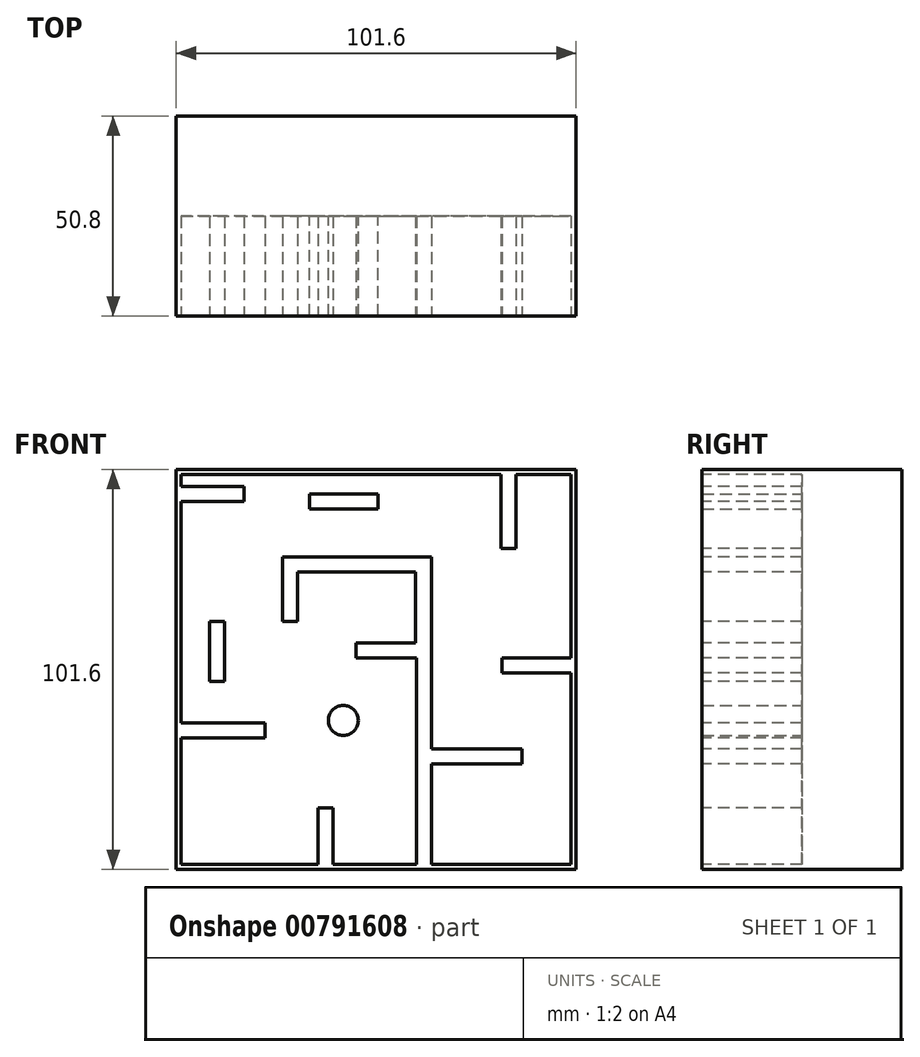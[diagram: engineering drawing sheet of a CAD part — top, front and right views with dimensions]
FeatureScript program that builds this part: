
annotation { "Feature Type Name" : "Feature", "Feature Type Description" : "" }
export const myFeature = defineFeature(function(context is Context, id is Id, definition is map)
    precondition{}
    {
        {
            var Q0;
            Q0=qCreatedBy(makeId("Front.planeOp"),FACE);
            var sketch = newSketch(context, id + "F0", { "sketchPlane" : qUnion([Q0])});
            skLineSegment(sketch, "E0.bottom", {"start": v(-45.67, 38.55) * mm, "end": v(55.93, 38.55) * mm});
            skLineSegment(sketch, "E0.top", {"start": v(-45.67, -63.05) * mm, "end": v(55.93, -63.05) * mm});
            skLineSegment(sketch, "E0.left", {"start": v(-45.67, 38.55) * mm, "end": v(-45.67, -63.05) * mm});
            skLineSegment(sketch, "E0.right", {"start": v(55.93, 38.55) * mm, "end": v(55.93, -63.05) * mm});
            skSolve(sketch);
        }
        {
            var Q0;
            Q0 = qSketchRegion(id + "F0", true);
            extrude(context, id + "F1", {"entities" : qUnion([Q0]), "depth" : 50.8 * mm, "offsetDistance" : 25.4 * mm});
        }
        {
            var Q0;
            Q0=makeQuery(id+"F1.opExtrude","CAP_FACE",FACE,{"disambiguationData":[OSD([sQuery(id+"F0.wireOp",EDGE,"E0.bottom"),sQuery(id+"F0.wireOp",EDGE,"E0.top"),sQuery(id+"F0.wireOp",EDGE,"E0.left"),sQuery(id+"F0.wireOp",EDGE,"E0.right")])],"isStart":false});
            var sketch = newSketch(context, id + "F2", { "sketchPlane" : qUnion([Q0])});
            skPoint(sketch, "E1.end.orphan", {"position": v(-45.67, -36.4) * mm});
            skLineSegment(sketch, "E2", {"start": v(-9.62, -63.05) * mm, "end": v(-9.62, -47.4) * mm});
            skPoint(sketch, "E2.startSnap0", {"position": v(-9.62, -34.5) * mm});
            skLineSegment(sketch, "E3", {"start": v(-9.62, -47.4) * mm, "end": v(-5.8, -47.4) * mm});
            skLineSegment(sketch, "E4", {"start": v(-5.8, -47.4) * mm, "end": v(-5.8, -63.05) * mm});
            skLineSegment(sketch, "E5", {"start": v(0, -9.31) * mm, "end": v(15.4, -9.31) * mm});
            skLineSegment(sketch, "E6", {"start": v(19.22, -9.31) * mm, "end": v(19.22, 16.32) * mm});
            skLineSegment(sketch, "E7", {"start": v(19.22, 16.32) * mm, "end": v(-18.6, 16.32) * mm});
            skLineSegment(sketch, "E8", {"start": v(-18.6, 16.32) * mm, "end": v(-18.6, 0) * mm});
            skLineSegment(sketch, "E9", {"start": v(0, -9.31) * mm, "end": v(0, -5.5) * mm});
            skLineSegment(sketch, "E10", {"start": v(0, -5.5) * mm, "end": v(15.1, -5.5) * mm});
            skLineSegment(sketch, "E11", {"start": v(15.1, -5.5) * mm, "end": v(15.1, 12.51) * mm});
            skLineSegment(sketch, "E12", {"start": v(15.1, 12.51) * mm, "end": v(-14.78, 12.51) * mm});
            skLineSegment(sketch, "E13", {"start": v(-14.78, 12.51) * mm, "end": v(-14.78, 0) * mm});
            skLineSegment(sketch, "E14", {"start": v(-14.78, 0) * mm, "end": v(-18.6, 0) * mm});
            skLineSegment(sketch, "E15", {"start": v(36.89, 38.55) * mm, "end": v(36.89, 18.45) * mm});
            skLineSegment(sketch, "E16", {"start": v(36.89, 18.45) * mm, "end": v(40.7, 18.45) * mm});
            skLineSegment(sketch, "E17", {"start": v(40.7, 18.45) * mm, "end": v(40.7, 38.55) * mm});
            skLineSegment(sketch, "E18", {"start": v(-45.67, 30.44) * mm, "end": v(-28.48, 30.44) * mm});
            skLineSegment(sketch, "E19", {"start": v(-28.48, 30.44) * mm, "end": v(-28.48, 34.25) * mm});
            skLineSegment(sketch, "E20", {"start": v(-45.67, 34.25) * mm, "end": v(-28.48, 34.25) * mm});
            skLineSegment(sketch, "E21", {"start": v(-37.16, 0) * mm, "end": v(-37.16, -15.24) * mm});
            skLineSegment(sketch, "E22", {"start": v(-37.16, -15.24) * mm, "end": v(-33.35, -15.24) * mm});
            skLineSegment(sketch, "E23", {"start": v(-33.35, -15.24) * mm, "end": v(-33.35, 0) * mm});
            skLineSegment(sketch, "E24", {"start": v(-33.35, 0) * mm, "end": v(-37.16, 0) * mm});
            skPoint(sketch, "E25.end.orphan", {"position": v(28.1, -9.31) * mm});
            skLineSegment(sketch, "E26", {"start": v(19.22, -9.31) * mm, "end": v(19.22, -63.05) * mm});
            skLineSegment(sketch, "E27", {"start": v(55.93, -9.31) * mm, "end": v(37.16, -9.31) * mm});
            skPoint(sketch, "E27.startSnap0", {"position": v(55.93, -12.25) * mm});
            skLineSegment(sketch, "E28", {"start": v(37.16, -9.31) * mm, "end": v(37.16, -13.12) * mm});
            skLineSegment(sketch, "E29", {"start": v(37.16, -13.12) * mm, "end": v(55.93, -13.12) * mm});
            skLineSegment(sketch, "E30", {"start": v(19.22, -36.18) * mm, "end": v(42.2, -36.18) * mm});
            skLineSegment(sketch, "E31", {"start": v(42.2, -36.18) * mm, "end": v(42.2, -32.37) * mm});
            skLineSegment(sketch, "E32", {"start": v(42.2, -32.37) * mm, "end": v(19.22, -32.37) * mm});
            skPoint(sketch, "E33.startSnap0", {"position": v(30.7, -32.37) * mm});
            skLineSegment(sketch, "E34", {"start": v(15.4, -9.31) * mm, "end": v(15.4, -63.05) * mm});
            skPoint(sketch, "E35.end.orphan", {"position": v(37.16, -63.05) * mm});
            skPoint(sketch, "E36.end.orphan", {"position": v(37.16, -49.37) * mm});
            skPoint(sketch, "E33.start.orphan", {"position": v(30.7, -63.05) * mm});
            skPoint(sketch, "E37.center.orphan", {"position": v(45.99, -49.37) * mm});
            skCircle(sketch, "E38", {"center": v(42.6, -53.74) * mm, "radius": 6.35 * mm});
            skPoint(sketch, "E39.orphan", {"position": v(-9.62, -32.6) * mm});
            skPoint(sketch, "E40.start.orphan", {"position": v(-9.62, -36.4) * mm});
            skLineSegment(sketch, "E41", {"start": v(-45.67, -25.84) * mm, "end": v(-23.04, -25.84) * mm});
            skLineSegment(sketch, "E42", {"start": v(-23.04, -25.84) * mm, "end": v(-23.04, -29.65) * mm});
            skLineSegment(sketch, "E43", {"start": v(-23.04, -29.65) * mm, "end": v(-45.67, -29.65) * mm});
            skLineSegment(sketch, "E44", {"start": v(-44.4, 30.44) * mm, "end": v(-44.4, -25.84) * mm});
            skLineSegment(sketch, "E45", {"start": v(-44.4, 37.28) * mm, "end": v(-44.4, 34.25) * mm});
            skLineSegment(sketch, "E46", {"start": v(-44.4, 37.28) * mm, "end": v(36.89, 37.28) * mm});
            skLineSegment(sketch, "E47", {"start": v(40.7, 37.28) * mm, "end": v(54.66, 37.28) * mm});
            skLineSegment(sketch, "E48", {"start": v(54.66, 37.28) * mm, "end": v(54.66, -9.31) * mm});
            skLineSegment(sketch, "E49", {"start": v(54.66, -13.12) * mm, "end": v(54.66, -61.78) * mm});
            skLineSegment(sketch, "E50", {"start": v(54.66, -61.78) * mm, "end": v(19.22, -61.78) * mm});
            skLineSegment(sketch, "E51", {"start": v(15.4, -61.78) * mm, "end": v(-5.8, -61.78) * mm});
            skLineSegment(sketch, "E52", {"start": v(-9.62, -61.78) * mm, "end": v(-44.4, -61.78) * mm});
            skLineSegment(sketch, "E53", {"start": v(-44.4, -61.78) * mm, "end": v(-44.4, -29.65) * mm});
            skSolve(sketch);
        }
        {
            var Q0;
            {var subQ10=sQuery(id+"F2.wireOp",EDGE,"E3");Q0=makeQuery(id+"F2.imprint","IMPRINT",FACE,{"disambiguationData":[TD([[makeQuery(id+"F2.imprint","IMPRINT",EDGE,{"derivedFrom":subQ10}),1.0]])]});}
            extrude(context, id + "F3", {"entities" : qUnion([Q0]), "operationType" : NewBodyOperationType.REMOVE, "oppositeDirection" : true, "depth" : 25.4 * mm, "offsetDistance" : 25.4 * mm});
        }
        {
            var Q0;
            Q0=makeQuery(id+"F3.boolean.opBoolean","SPLIT",FACE,{"disambiguationData":[TD([makeQuery(id+"F3.opExtrude","SWEPT_FACE",FACE,{"disambiguationData":[OSD([sQuery(id+"F2.wireOp",EDGE,"E38")])]})])],"derivedFrom":makeQuery(id+"F1.opExtrude","CAP_FACE",FACE,{"disambiguationData":[OSD([sQuery(id+"F0.wireOp",EDGE,"E0.bottom"),sQuery(id+"F0.wireOp",EDGE,"E0.top"),sQuery(id+"F0.wireOp",EDGE,"E0.left"),sQuery(id+"F0.wireOp",EDGE,"E0.right")])],"isStart":false})});
            extrude(context, id + "F4", {"entities" : qUnion([Q0]), "operationType" : NewBodyOperationType.REMOVE, "oppositeDirection" : true, "depth" : 25.4 * mm, "offsetDistance" : 25.4 * mm});
        }
        {
            var Q0;
            Q0=makeQuery(id+"F4.boolean.opBoolean","MERGE",FACE,{"derivedFrom":[makeQuery(id+"F3.boolean.opBoolean","COPY",FACE,{"derivedFrom":makeQuery(id+"F3.opExtrude","CAP_FACE",FACE,{"disambiguationData":[OSD([sQuery(id+"F2.wireOp",EDGE,"E2"),sQuery(id+"F2.wireOp",EDGE,"E3"),sQuery(id+"F2.wireOp",EDGE,"E4"),sQuery(id+"F2.wireOp",EDGE,"E5"),sQuery(id+"F2.wireOp",EDGE,"E6"),sQuery(id+"F2.wireOp",EDGE,"E7"),sQuery(id+"F2.wireOp",EDGE,"E8"),sQuery(id+"F2.wireOp",EDGE,"E9"),sQuery(id+"F2.wireOp",EDGE,"E10"),sQuery(id+"F2.wireOp",EDGE,"E11"),sQuery(id+"F2.wireOp",EDGE,"E12"),sQuery(id+"F2.wireOp",EDGE,"E13"),sQuery(id+"F2.wireOp",EDGE,"E14"),sQuery(id+"F2.wireOp",EDGE,"E15"),sQuery(id+"F2.wireOp",EDGE,"E16"),sQuery(id+"F2.wireOp",EDGE,"E17"),sQuery(id+"F2.wireOp",EDGE,"E18"),sQuery(id+"F2.wireOp",EDGE,"E19"),sQuery(id+"F2.wireOp",EDGE,"E20"),sQuery(id+"F2.wireOp",EDGE,"E21"),sQuery(id+"F2.wireOp",EDGE,"E22"),sQuery(id+"F2.wireOp",EDGE,"E23"),sQuery(id+"F2.wireOp",EDGE,"E24"),sQuery(id+"F2.wireOp",EDGE,"E26"),sQuery(id+"F2.wireOp",EDGE,"E27"),sQuery(id+"F2.wireOp",EDGE,"E28"),sQuery(id+"F2.wireOp",EDGE,"E29"),sQuery(id+"F2.wireOp",EDGE,"E30"),sQuery(id+"F2.wireOp",EDGE,"E31"),sQuery(id+"F2.wireOp",EDGE,"E32"),sQuery(id+"F2.wireOp",EDGE,"E34"),sQuery(id+"F2.wireOp",EDGE,"E38"),sQuery(id+"F2.wireOp",EDGE,"E41"),sQuery(id+"F2.wireOp",EDGE,"E42"),sQuery(id+"F2.wireOp",EDGE,"E43"),sQuery(id+"F2.wireOp",EDGE,"E44"),sQuery(id+"F2.wireOp",EDGE,"E45"),sQuery(id+"F2.wireOp",EDGE,"E46"),sQuery(id+"F2.wireOp",EDGE,"E47"),sQuery(id+"F2.wireOp",EDGE,"E48"),sQuery(id+"F2.wireOp",EDGE,"E49"),sQuery(id+"F2.wireOp",EDGE,"E50"),sQuery(id+"F2.wireOp",EDGE,"E51"),sQuery(id+"F2.wireOp",EDGE,"E52"),sQuery(id+"F2.wireOp",EDGE,"E53")])],"isStart":false})}),makeQuery(id+"F4.opExtrude","CAP_FACE",FACE,{"disambiguationData":[OSD([sQuery(id+"F0.wireOp",EDGE,"E0.bottom"),sQuery(id+"F0.wireOp",EDGE,"E0.top"),sQuery(id+"F0.wireOp",EDGE,"E0.left"),sQuery(id+"F0.wireOp",EDGE,"E0.right")])],"isStart":false})]});
            var sketch = newSketch(context, id + "F5", { "sketchPlane" : qUnion([Q0])});
            skCircle(sketch, "E54", {"center": v(-3.22, -25.2) * mm, "radius": 3.81 * mm});
            skSolve(sketch);
        }
        {
            var Q0;
            Q0 = qSketchRegion(id + "F5", true);
            extrude(context, id + "F6", {"entities" : qUnion([Q0]), "operationType" : NewBodyOperationType.ADD, "depth" : 25.4 * mm, "offsetDistance" : 25.4 * mm});
        }
        {
            var Q0;
            Q0=makeQuery(id+"F4.boolean.opBoolean","MERGE",FACE,{"derivedFrom":[makeQuery(id+"F3.boolean.opBoolean","COPY",FACE,{"derivedFrom":makeQuery(id+"F3.opExtrude","CAP_FACE",FACE,{"disambiguationData":[OSD([sQuery(id+"F2.wireOp",EDGE,"E2"),sQuery(id+"F2.wireOp",EDGE,"E3"),sQuery(id+"F2.wireOp",EDGE,"E4"),sQuery(id+"F2.wireOp",EDGE,"E5"),sQuery(id+"F2.wireOp",EDGE,"E6"),sQuery(id+"F2.wireOp",EDGE,"E7"),sQuery(id+"F2.wireOp",EDGE,"E8"),sQuery(id+"F2.wireOp",EDGE,"E9"),sQuery(id+"F2.wireOp",EDGE,"E10"),sQuery(id+"F2.wireOp",EDGE,"E11"),sQuery(id+"F2.wireOp",EDGE,"E12"),sQuery(id+"F2.wireOp",EDGE,"E13"),sQuery(id+"F2.wireOp",EDGE,"E14"),sQuery(id+"F2.wireOp",EDGE,"E15"),sQuery(id+"F2.wireOp",EDGE,"E16"),sQuery(id+"F2.wireOp",EDGE,"E17"),sQuery(id+"F2.wireOp",EDGE,"E18"),sQuery(id+"F2.wireOp",EDGE,"E19"),sQuery(id+"F2.wireOp",EDGE,"E20"),sQuery(id+"F2.wireOp",EDGE,"E21"),sQuery(id+"F2.wireOp",EDGE,"E22"),sQuery(id+"F2.wireOp",EDGE,"E23"),sQuery(id+"F2.wireOp",EDGE,"E24"),sQuery(id+"F2.wireOp",EDGE,"E26"),sQuery(id+"F2.wireOp",EDGE,"E27"),sQuery(id+"F2.wireOp",EDGE,"E28"),sQuery(id+"F2.wireOp",EDGE,"E29"),sQuery(id+"F2.wireOp",EDGE,"E30"),sQuery(id+"F2.wireOp",EDGE,"E31"),sQuery(id+"F2.wireOp",EDGE,"E32"),sQuery(id+"F2.wireOp",EDGE,"E34"),sQuery(id+"F2.wireOp",EDGE,"E38"),sQuery(id+"F2.wireOp",EDGE,"E41"),sQuery(id+"F2.wireOp",EDGE,"E42"),sQuery(id+"F2.wireOp",EDGE,"E43"),sQuery(id+"F2.wireOp",EDGE,"E44"),sQuery(id+"F2.wireOp",EDGE,"E45"),sQuery(id+"F2.wireOp",EDGE,"E46"),sQuery(id+"F2.wireOp",EDGE,"E47"),sQuery(id+"F2.wireOp",EDGE,"E48"),sQuery(id+"F2.wireOp",EDGE,"E49"),sQuery(id+"F2.wireOp",EDGE,"E50"),sQuery(id+"F2.wireOp",EDGE,"E51"),sQuery(id+"F2.wireOp",EDGE,"E52"),sQuery(id+"F2.wireOp",EDGE,"E53")])],"isStart":false})}),makeQuery(id+"F4.opExtrude","CAP_FACE",FACE,{"disambiguationData":[OSD([sQuery(id+"F0.wireOp",EDGE,"E0.bottom"),sQuery(id+"F0.wireOp",EDGE,"E0.top"),sQuery(id+"F0.wireOp",EDGE,"E0.left"),sQuery(id+"F0.wireOp",EDGE,"E0.right")])],"isStart":false})]});
            var sketch = newSketch(context, id + "F7", { "sketchPlane" : qUnion([Q0])});
            skPoint(sketch, "E55.end.orphan", {"position": v(5.78, 27.43) * mm});
            skPoint(sketch, "E55.start.orphan", {"position": v(5.78, 33.26) * mm});
            skLineSegment(sketch, "E56.bottom", {"start": v(-11.73, 32.32) * mm, "end": v(5.63, 32.32) * mm});
            skLineSegment(sketch, "E56.top", {"start": v(-11.73, 28.5) * mm, "end": v(5.63, 28.5) * mm});
            skLineSegment(sketch, "E56.left", {"start": v(-11.73, 32.32) * mm, "end": v(-11.73, 28.5) * mm});
            skLineSegment(sketch, "E56.right", {"start": v(5.63, 32.32) * mm, "end": v(5.63, 28.5) * mm});
            skSolve(sketch);
        }
        {
            var Q0;
            Q0 = qSketchRegion(id + "F7", true);
            extrude(context, id + "F8", {"entities" : qUnion([Q0]), "operationType" : NewBodyOperationType.ADD, "depth" : 25.4 * mm, "offsetDistance" : 25.4 * mm});
        }
    });
